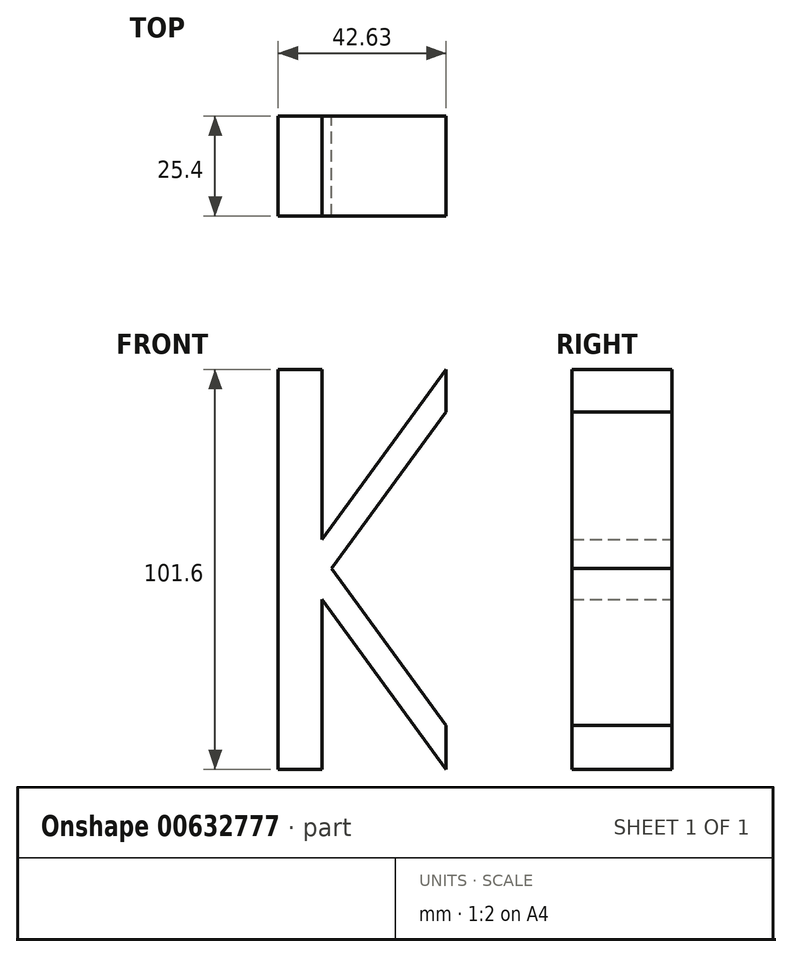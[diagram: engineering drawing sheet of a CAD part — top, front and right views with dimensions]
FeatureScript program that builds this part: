
annotation { "Feature Type Name" : "Feature", "Feature Type Description" : "" }
export const myFeature = defineFeature(function(context is Context, id is Id, definition is map)
    precondition{}
    {
        {
            var Q0;
            Q0=qCreatedBy(makeId("Front.planeOp"),FACE);
            var sketch = newSketch(context, id + "F0", { "sketchPlane" : qUnion([Q0])});
            skLineSegment(sketch, "E0.bottom", {"start": v(5.58, -50.8) * mm, "end": v(-5.58, -50.8) * mm});
            skLineSegment(sketch, "E0.top", {"start": v(5.58, 50.8) * mm, "end": v(-5.58, 50.8) * mm});
            skLineSegment(sketch, "E0.left", {"start": v(5.58, -50.8) * mm, "end": v(5.58, 50.8) * mm});
            skLineSegment(sketch, "E0.right", {"start": v(-5.58, -50.8) * mm, "end": v(-5.58, 50.8) * mm});
            skPoint(sketch, "E0.middle", {"position": v(0, 0) * mm});
            skLineSegment(sketch, "E1.bottom", {"start": v(5.58, -50.8) * mm, "end": v(37.05, -50.8) * mm});
            skLineSegment(sketch, "E1.top", {"start": v(5.58, 50.8) * mm, "end": v(37.05, 50.8) * mm});
            skLineSegment(sketch, "E1.right", {"start": v(37.05, -50.8) * mm, "end": v(37.05, 50.8) * mm});
            skPoint(sketch, "E1.middle", {"position": v(21.32, 0) * mm});
            skLineSegment(sketch, "E2.bottom", {"start": v(50.66, -50.8) * mm, "end": v(9.27, -50.8) * mm});
            skLineSegment(sketch, "E2.top", {"start": v(50.66, 50.8) * mm, "end": v(9.27, 50.8) * mm});
            skLineSegment(sketch, "E2.left", {"start": v(50.66, -50.8) * mm, "end": v(50.66, 50.8) * mm});
            skLineSegment(sketch, "E2.right", {"start": v(9.27, -50.8) * mm, "end": v(9.27, 50.8) * mm});
            skPoint(sketch, "E2.middle", {"position": v(29.97, 0) * mm});
            skPoint(sketch, "E2.cornerSnap0", {"position": v(21.32, -50.8) * mm});
            skLineSegment(sketch, "E3", {"start": v(0, 0) * mm, "end": v(37.05, 50.8) * mm});
            skLineSegment(sketch, "E4", {"start": v(50.66, 50.8) * mm, "end": v(37.05, 50.8) * mm});
            skLineSegment(sketch, "E5", {"start": v(0, 0) * mm, "end": v(37.05, -50.8) * mm});
            skLineSegment(sketch, "E6.0", {"start": v(5.13, -3.74) * mm, "end": v(42.18, 47.06) * mm});
            skLineSegment(sketch, "E7.0", {"start": v(5.34, 3.9) * mm, "end": v(42.38, -46.9) * mm});
            skSolve(sketch);
        }
        {
            var Q0;
            {var subQ2=sQuery(id+"F0.wireOp",EDGE,"E0.bottom");Q0=makeQuery(id+"F0.imprint","IMPRINT",FACE,{"disambiguationData":[TD([[makeQuery(id+"F0.imprint","IMPRINT",EDGE,{"derivedFrom":subQ2}),-1.0]])]});}
            var Q1;
            {var subQ3=sQuery(id+"F0.wireOp",EDGE,"E6.0");var subQ5=sQuery(id+"F0.wireOp",EDGE,"E2.right");var subQ6=makeQuery(id+"F0.imprint","INTERSECT",VERTEX,{"derivedFrom":[subQ5,subQ3]});Q1=makeQuery(id+"F0.imprint","IMPRINT",FACE,{"disambiguationData":[TD([[makeQuery(id+"F0.imprint","IMPRINT",EDGE,{"disambiguationData":[TD([[subQ6,-1.0]])],"derivedFrom":subQ5}),-1.0]])]});}
            var Q2;
            {var subQ0=sQuery(id+"F0.wireOp",EDGE,"E5");var subQ5=sQuery(id+"F0.wireOp",EDGE,"E2.right");var subQ6=makeQuery(id+"F0.imprint","INTERSECT",VERTEX,{"derivedFrom":[subQ5,subQ0]});Q2=makeQuery(id+"F0.imprint","IMPRINT",FACE,{"disambiguationData":[TD([[makeQuery(id+"F0.imprint","IMPRINT",EDGE,{"disambiguationData":[TD([[subQ6,-1.0]])],"derivedFrom":subQ5}),-1.0]])]});}
            var Q3;
            {var subQ0=sQuery(id+"F0.wireOp",EDGE,"E6.0");var subQ1=sQuery(id+"F0.wireOp",EDGE,"E0.left");var subQ2=makeQuery(id+"F0.imprint","INTERSECT",VERTEX,{"derivedFrom":[subQ1,subQ0]});Q3=makeQuery(id+"F0.imprint","IMPRINT",FACE,{"disambiguationData":[TD([[makeQuery(id+"F0.imprint","IMPRINT",EDGE,{"disambiguationData":[TD([[subQ2,1.0]])],"derivedFrom":subQ1}),-1.0]])]});}
            var Q4;
            {var subQ3=sQuery(id+"F0.wireOp",EDGE,"E7.0");var subQ7=sQuery(id+"F0.wireOp",EDGE,"E0.left");var subQ8=makeQuery(id+"F0.imprint","INTERSECT",VERTEX,{"derivedFrom":[subQ7,subQ3]});Q4=makeQuery(id+"F0.imprint","IMPRINT",FACE,{"disambiguationData":[TD([[makeQuery(id+"F0.imprint","IMPRINT",EDGE,{"disambiguationData":[TD([[subQ8,-1.0]])],"derivedFrom":subQ7}),-1.0]])]});}
            var Q5;
            {var subQ0=sQuery(id+"F0.wireOp",EDGE,"E0.left");var subQ4=makeQuery(id+"F0.imprint","INTERSECT",VERTEX,{"derivedFrom":[subQ0,sQuery(id+"F0.wireOp",EDGE,"E6.0")]});Q5=makeQuery(id+"F0.imprint","IMPRINT",FACE,{"disambiguationData":[TD([[makeQuery(id+"F0.imprint","IMPRINT",EDGE,{"disambiguationData":[TD([[subQ4,1.0]])],"derivedFrom":subQ0}),1.0]])]});}
            var Q6;
            {var subQ0=sQuery(id+"F0.wireOp",EDGE,"E6.0");var subQ1=sQuery(id+"F0.wireOp",EDGE,"E0.left");var subQ2=makeQuery(id+"F0.imprint","INTERSECT",VERTEX,{"derivedFrom":[subQ1,subQ0]});Q6=makeQuery(id+"F0.imprint","IMPRINT",FACE,{"disambiguationData":[TD([[makeQuery(id+"F0.imprint","IMPRINT",EDGE,{"disambiguationData":[TD([[subQ2,-1.0]])],"derivedFrom":subQ1}),-1.0]])]});}
            extrude(context, id + "F1", {"entities" : qUnion([Q0, Q1, Q2, Q3, Q4, Q5, Q6]), "depth" : 25.4 * mm, "offsetDistance" : 25.4 * mm});
        }
    });
